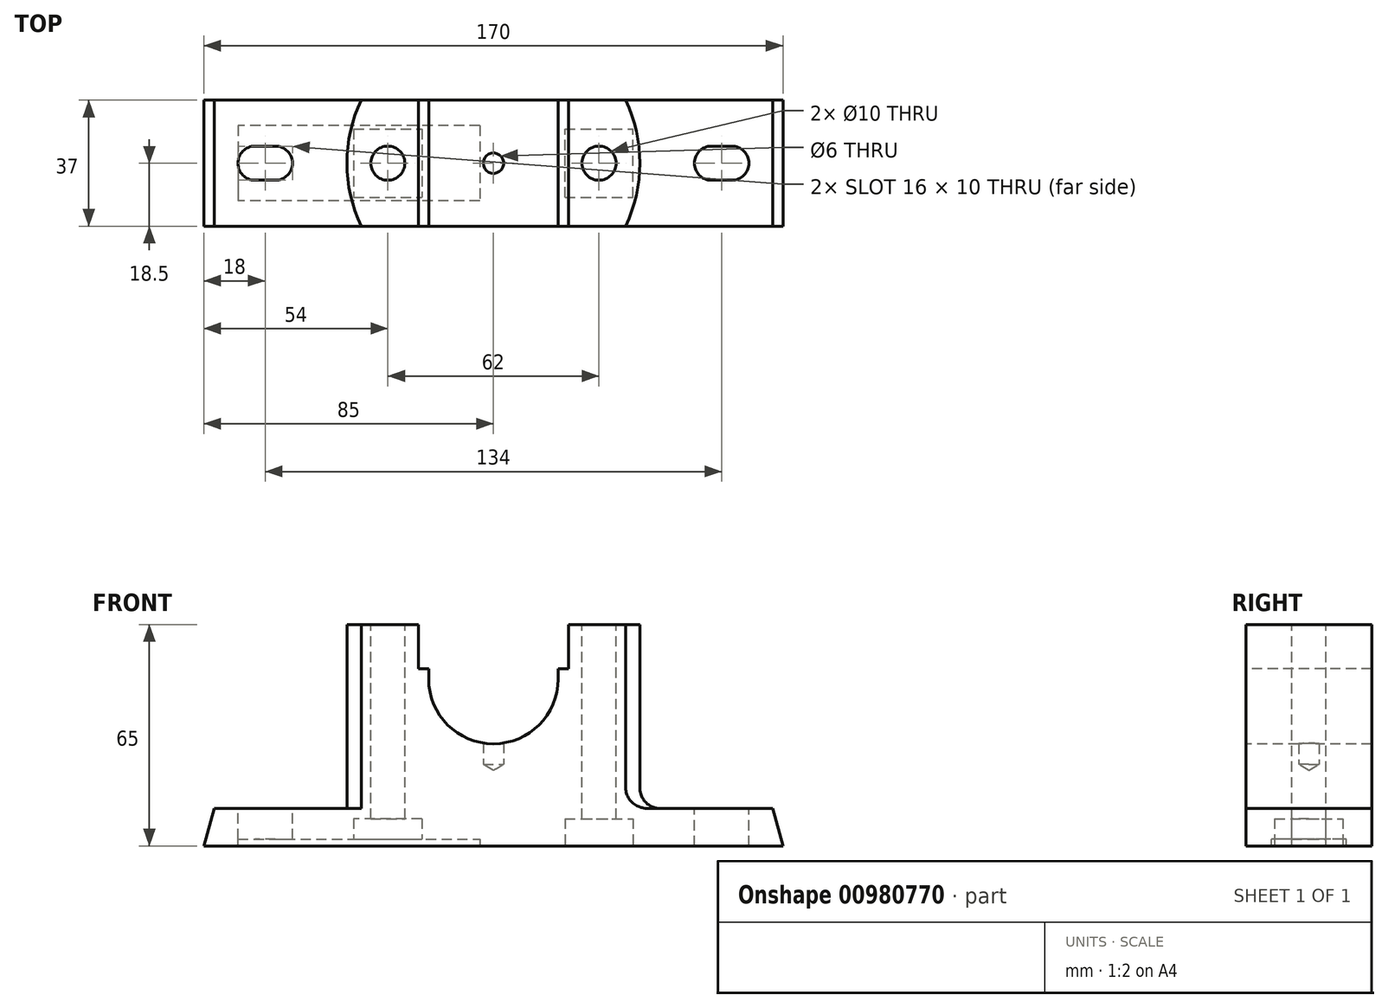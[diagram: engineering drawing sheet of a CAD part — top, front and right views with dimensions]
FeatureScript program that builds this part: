
annotation { "Feature Type Name" : "Feature", "Feature Type Description" : "" }
export const myFeature = defineFeature(function(context is Context, id is Id, definition is map)
    precondition{}
    {
        {
            var Q0;
            Q0=qCreatedBy(makeId("Front.planeOp"),FACE);
            var sketch = newSketch(context, id + "F0", { "sketchPlane" : qUnion([Q0])});
            skLineSegment(sketch, "E0", {"start": v(-85, 0) * mm, "end": v(85, 0) * mm});
            skLineSegment(sketch, "E1", {"start": v(-85, 0) * mm, "end": v(-82, 11) * mm});
            skLineSegment(sketch, "E2", {"start": v(0, 0) * mm, "end": v(0, 40.06) * mm, "construction": true});
            skLineSegment(sketch, "E3.MirrorCS", {"start": v(85, 0) * mm, "end": v(82, 11) * mm});
            skLineSegment(sketch, "E4", {"start": v(-82, 11) * mm, "end": v(82, 11) * mm});
            skSolve(sketch);
        }
        {
            var Q0;
            Q0 = qSketchRegion(id + "F0", true);
            extrude(context, id + "F1", {"entities" : qUnion([Q0]), "endBound" : BoundingType.SYMMETRIC, "depth" : 37 * mm, "offsetDistance" : 25 * mm});
        }
        {
            var Q0;
            Q0=makeQuery(id+"F1.opExtrude","SWEPT_FACE",FACE,{"disambiguationData":[OSD([sQuery(id+"F0.wireOp",EDGE,"E4")])]});
            var sketch = newSketch(context, id + "F2", { "sketchPlane" : qUnion([Q0])});
            skArc(sketch, "E5", {"start": v(-38.82, 18.5) * mm, "mid": v(-43, 0) * mm, "end": v(-38.82, -18.5) * mm});
            skLineSegment(sketch, "E6.0", {"start": v(-38.82, 18.5) * mm, "end": v(38.82, 18.5) * mm});
            skLineSegment(sketch, "E6.1", {"start": v(-38.82, -18.5) * mm, "end": v(38.82, -18.5) * mm});
            skPoint(sketch, "E7.orphan", {"position": v(-82, 18.5) * mm});
            skPoint(sketch, "E8.orphan", {"position": v(82, 18.5) * mm});
            skPoint(sketch, "E9.orphan", {"position": v(82, -18.5) * mm});
            skArc(sketch, "E10.trimOffspring", {"start": v(38.82, -18.5) * mm, "mid": v(43, 0) * mm, "end": v(38.82, 18.5) * mm});
            skPoint(sketch, "E11.orphan", {"position": v(-82, -18.5) * mm});
            skSolve(sketch);
        }
        {
            var Q0;
            Q0=makeQuery(id+"F2.imprint","IMPRINT",FACE,{"disambiguationData":[TD([[makeQuery(id+"F2.imprint","IMPRINT",EDGE,{"derivedFrom":sQuery(id+"F2.wireOp",EDGE,"E5")}),1.0]])]});
            extrude(context, id + "F3", {"entities" : qUnion([Q0]), "operationType" : NewBodyOperationType.ADD, "depth" : 54 * mm, "offsetDistance" : 25 * mm});
        }
        {
            var Q0;
            Q0=qCreatedBy(makeId("Front.planeOp"),FACE);
            var sketch = newSketch(context, id + "F4", { "sketchPlane" : qUnion([Q0])});
            skLineSegment(sketch, "E12", {"start": v(-22, 65) * mm, "end": v(-22, 52) * mm});
            skLineSegment(sketch, "E13", {"start": v(-22, 52) * mm, "end": v(-19, 52) * mm});
            skLineSegment(sketch, "E14", {"start": v(-19, 52) * mm, "end": v(-19, 49) * mm});
            skArc(sketch, "E15", {"start": v(-19, 49) * mm, "mid": v(0, 30) * mm, "end": v(19, 49) * mm});
            skLineSegment(sketch, "E16.MirrorCS", {"start": v(22, 52) * mm, "end": v(19, 52) * mm});
            skLineSegment(sketch, "E17.MirrorCS", {"start": v(22, 65) * mm, "end": v(22, 52) * mm});
            skLineSegment(sketch, "E18.MirrorCS", {"start": v(19, 52) * mm, "end": v(19, 49) * mm});
            skLineSegment(sketch, "E19", {"start": v(-22, 65) * mm, "end": v(22, 65) * mm});
            skSolve(sketch);
        }
        {
            var Q0;
            Q0 = qSketchRegion(id + "F4", true);
            extrude(context, id + "F5", {"entities" : qUnion([Q0]), "operationType" : NewBodyOperationType.REMOVE, "endBound" : BoundingType.SYMMETRIC, "oppositeDirection" : true, "depth" : 97 * mm, "offsetDistance" : 25 * mm});
        }
        {
            var Q0;
            {var subQ0=sQuery(id+"F2.wireOp",EDGE,"E5");var subQ5=sQuery(id+"F2.wireOp",EDGE,"E6.0");var subQ6=sQuery(id+"F2.wireOp",EDGE,"E6.1");Q0=makeQuery(id+"F5.boolean.opBoolean","SPLIT",FACE,{"disambiguationData":[TD([makeQuery(id+"F3.opExtrude","SWEPT_FACE",FACE,{"disambiguationData":[OSD([subQ0])]})])],"derivedFrom":makeQuery(id+"F3.opExtrude","CAP_FACE",FACE,{"disambiguationData":[OSD([subQ0,subQ5,subQ6,sQuery(id+"F2.wireOp",EDGE,"E10.trimOffspring")])],"isStart":false})});}
            var sketch = newSketch(context, id + "F6", { "sketchPlane" : qUnion([Q0])});
            skLineSegment(sketch, "E20", {"start": v(0, 0) * mm, "end": v(0, 69.04) * mm, "construction": true});
            skCircle(sketch, "E21", {"center": v(-31, 0) * mm, "radius": 5 * mm});
            skCircle(sketch, "E22.MirrorC", {"center": v(31, 0) * mm, "radius": 5 * mm});
            skSolve(sketch);
        }
        {
            var Q0;
            Q0 = qSketchRegion(id + "F6", true);
            extrude(context, id + "F7", {"entities" : qUnion([Q0]), "operationType" : NewBodyOperationType.REMOVE, "endBound" : BoundingType.THROUGH_ALL, "oppositeDirection" : true, "depth" : 25 * mm, "offsetDistance" : 25 * mm});
        }
        {
            var Q0;
            Q0=makeQuery(id+"F1.opExtrude","SWEPT_FACE",FACE,{"disambiguationData":[OSD([sQuery(id+"F0.wireOp",EDGE,"E0")])]});
            var sketch = newSketch(context, id + "F8", { "sketchPlane" : qUnion([Q0])});
            skLineSegment(sketch, "E23.bottom", {"start": v(-21, 10) * mm, "end": v(-41, 10) * mm});
            skLineSegment(sketch, "E23.top", {"start": v(-21, -10) * mm, "end": v(-41, -10) * mm});
            skLineSegment(sketch, "E23.left", {"start": v(-21, 10) * mm, "end": v(-21, -10) * mm});
            skLineSegment(sketch, "E23.right", {"start": v(-41, 10) * mm, "end": v(-41, -10) * mm});
            skPoint(sketch, "E23.middle", {"position": v(-31, 0) * mm});
            skLineSegment(sketch, "E24.MirrorCS", {"start": v(21, 10) * mm, "end": v(21, -10) * mm});
            skLineSegment(sketch, "E25.MirrorCS", {"start": v(21, 10) * mm, "end": v(41, 10) * mm});
            skLineSegment(sketch, "E26.MirrorCS", {"start": v(41, 10) * mm, "end": v(41, -10) * mm});
            skLineSegment(sketch, "E27.MirrorCS", {"start": v(21, -10) * mm, "end": v(41, -10) * mm});
            skSolve(sketch);
        }
        {
            var Q0;
            Q0 = qSketchRegion(id + "F8", true);
            extrude(context, id + "F9", {"entities" : qUnion([Q0]), "operationType" : NewBodyOperationType.REMOVE, "oppositeDirection" : true, "depth" : 8 * mm, "offsetDistance" : 25 * mm});
        }
        {
            var Q0;
            Q0=qCreatedBy(makeId("Front.planeOp"),FACE);
            var sketch = newSketch(context, id + "F10", { "sketchPlane" : qUnion([Q0])});
            skLineSegment(sketch, "E28", {"start": v(-75, 0) * mm, "end": v(-75, 2) * mm});
            skLineSegment(sketch, "E29", {"start": v(-75, 2) * mm, "end": v(-4, 2) * mm});
            skLineSegment(sketch, "E30", {"start": v(-4, 2) * mm, "end": v(-4, 0) * mm});
            skLineSegment(sketch, "E31", {"start": v(-4, 0) * mm, "end": v(-75, 0) * mm});
            skLineSegment(sketch, "E32", {"start": v(0, 0) * mm, "end": v(0, 73.2) * mm, "construction": true});
            skLineSegment(sketch, "E33", {"start": v(0, 73.2) * mm, "end": v(-67, 73.2) * mm, "construction": true});
            skLineSegment(sketch, "E34", {"start": v(-67, 73.2) * mm, "end": v(-67, 9.2) * mm, "construction": true});
            skLineSegment(sketch, "E35", {"start": v(-67, 9.2) * mm, "end": v(-75, 9.2) * mm, "construction": true});
            skLineSegment(sketch, "E36", {"start": v(-75, 9.2) * mm, "end": v(-59, 9.2) * mm, "construction": true});
            skSolve(sketch);
        }
        {
            var Q0;
            Q0 = qSketchRegion(id + "F10", true);
            extrude(context, id + "F11", {"entities" : qUnion([Q0]), "operationType" : NewBodyOperationType.REMOVE, "endBound" : BoundingType.SYMMETRIC, "oppositeDirection" : true, "depth" : 22 * mm, "offsetDistance" : 25 * mm});
        }
        {
            var Q0;
            {var subQ0=sQuery(id+"F0.wireOp",EDGE,"E4");var subQ2=sQuery(id+"F0.wireOp",EDGE,"E1");Q0=makeQuery(id+"F3.boolean.opBoolean","SPLIT",FACE,{"disambiguationData":[TD([makeQuery(id+"F1.opExtrude","SWEPT_FACE",FACE,{"disambiguationData":[OSD([subQ2])]})])],"derivedFrom":makeQuery(id+"F1.opExtrude","SWEPT_FACE",FACE,{"disambiguationData":[OSD([subQ0])]})});}
            var sketch = newSketch(context, id + "F12", { "sketchPlane" : qUnion([Q0])});
            skLineSegment(sketch, "E37", {"start": v(-70, 0) * mm, "end": v(-64, 0) * mm});
            skArc(sketch, "E38.0.startCap", {"start": v(-70, -5) * mm, "mid": v(-75, 0) * mm, "end": v(-70, 5) * mm});
            skArc(sketch, "E38.0.endCap", {"start": v(-64, 5) * mm, "mid": v(-59, 0) * mm, "end": v(-64, -5) * mm});
            skLineSegment(sketch, "E38.0.left", {"start": v(-70, 5) * mm, "end": v(-64, 5) * mm});
            skLineSegment(sketch, "E38.0.right", {"start": v(-70, -5) * mm, "end": v(-64, -5) * mm});
            skLineSegment(sketch, "E39", {"start": v(-67, 0) * mm, "end": v(-67, 10.76) * mm, "construction": true});
            skLineSegment(sketch, "E40", {"start": v(-59, 0) * mm, "end": v(-59, 0) * mm});
            skLineSegment(sketch, "E41.MirrorCS", {"start": v(70, 0) * mm, "end": v(64, 0) * mm});
            skLineSegment(sketch, "E42.MirrorCS", {"start": v(70, 5) * mm, "end": v(64, 5) * mm});
            skLineSegment(sketch, "E43.MirrorCS", {"start": v(70, -5) * mm, "end": v(64, -5) * mm});
            skArc(sketch, "E44.MirrorCS", {"start": v(64, 5) * mm, "mid": v(59, 0) * mm, "end": v(64, -5) * mm});
            skLineSegment(sketch, "E45.MirrorCS", {"start": v(59, 0) * mm, "end": v(59, 0) * mm});
            skArc(sketch, "E46.MirrorCS", {"start": v(70, -5) * mm, "mid": v(75, 0) * mm, "end": v(70, 5) * mm});
            skSolve(sketch);
        }
        {
            var Q0;
            Q0 = qSketchRegion(id + "F12", true);
            extrude(context, id + "F13", {"entities" : qUnion([Q0]), "operationType" : NewBodyOperationType.REMOVE, "endBound" : BoundingType.THROUGH_ALL, "oppositeDirection" : true, "depth" : 25 * mm, "offsetDistance" : 25 * mm});
        }
        {
            var Q0;
            Q0=qCreatedBy(makeId("Front.planeOp"),FACE);
            var sketch = newSketch(context, id + "F14", { "sketchPlane" : qUnion([Q0])});
            skLineSegment(sketch, "E47", {"start": v(0, 31.8) * mm, "end": v(0, 22.2) * mm});
            skLineSegment(sketch, "E48", {"start": v(0, 22.2) * mm, "end": v(3, 24) * mm});
            skLineSegment(sketch, "E49", {"start": v(3, 24) * mm, "end": v(3, 31.8) * mm});
            skLineSegment(sketch, "E50", {"start": v(3, 31.8) * mm, "end": v(0, 31.8) * mm});
            skSolve(sketch);
        }
        {
            var Q0;
            Q0 = qSketchRegion(id + "F14", true);
            var Q1;
            Q1=sQuery(id+"F14.wireOp",EDGE,"E47");
            revolve(context, id + "F15", {"operationType" : NewBodyOperationType.REMOVE, "surfaceOperationType" : NewSurfaceOperationType.NEW, "entities" : qUnion([Q0]), "axis" : qUnion([Q1]), "revolveType" : RevolveType.FULL, "oppositeDirection" : true});
        }
        {
            var Q0;
            Q0=makeQuery(id+"F14.imprint","IMPRINT",FACE,{"disambiguationData":[TD([[makeQuery(id+"F14.imprint","IMPRINT",EDGE,{"derivedFrom":sQuery(id+"F14.wireOp",EDGE,"E47")}),1.0]])]});
            var Q1;
            Q1=sQuery(id+"F14.wireOp",EDGE,"E47");
            revolve(context, id + "F16", {"operationType" : NewBodyOperationType.REMOVE, "surfaceOperationType" : NewSurfaceOperationType.NEW, "entities" : qUnion([Q0]), "axis" : qUnion([Q1]), "revolveType" : RevolveType.FULL, "oppositeDirection" : true});
        }
        {
            var Q0;
            Q0=makeQuery(id+"F3.opExtrude","CAP_EDGE",EDGE,{"disambiguationData":[OSD([sQuery(id+"F2.wireOp",EDGE,"E10.trimOffspring")])],"isStart":true});
            var Q1;
            Q1=makeQuery(id+"F3.opExtrude","CAP_EDGE",EDGE,{"disambiguationData":[OSD([sQuery(id+"F2.wireOp",EDGE,"E5")])],"isStart":true});
            fillet(context, id + "F17", {"entities" : qUnion([Q0, Q1]), "radius" : 6 * mm, "tangentPropagation" : true, "allowEdgeOverflow" : false});
        }
    });
